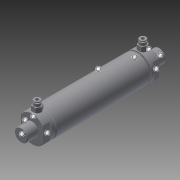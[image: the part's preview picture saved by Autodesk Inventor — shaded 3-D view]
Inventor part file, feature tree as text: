
AUTODESK INVENTOR PART (.ipt)
format: ipt  version: 2014 SP1 (Build 180222100, 222)  size: 331,776 bytes
history: native  units: in
note: dims shown in document units (in); Inventor stores cm internally (conversion verified against a paired STEP export)
features: other x3, imported_body x3, mirror x1
ambient origin geometry x8: Origin, YZ Plane, XZ Plane, XY Plane, X Axis, Y Axis, Z Axis, Center Point
bodies: Body1 (feature_tree), Body2 (feature_tree), Body3 (feature_tree)
feature tree (7):
  other  "Port"
  other  "Pneumatic Reservoir"
  other  "Port_1"
  mirror  "Mirror1"
  imported_body  "Base1"
  imported_body  "Base2"
  imported_body  "Base3"
